# Revit family: Trap-FloorMounted-Vitra-OriginSeries-A45161
name_source: partatom
category: Plumbing Fixtures
revit_build: Autodesk Revit 2017 (Build: 20160225_1515(x64)
units: mm (PartAtom-declared; Revit-internal decimal feet)

## family parameters
Cut with Voids When Loaded = No
Host = Face
OmniClass Number = 23.45.55.17
OmniClass Title = Mixing Faucets
Part Type = Normal
Room Calculation Point = No
Round Connector Dimension = Use Diameter
Shared = Yes

## types (2) — shared parameters
BIMobject category = Sanitary - Taps & Mixers
CW Connection = Yes
Connection Diameter (mm) = 10 mm  [stored 0.0328084 ft]
Default Elevation = 850 mm  [stored 2.78871 ft]
Depth(mm) = 340 mm  [stored 1.11549 ft]
Description = Plural Floor Siphon Set - Long
Design country = Turkey
HW Connection = Yes
Height(mm) = 715 mm
IFC Classification = Sanitary Terminal
Manufacturer = Vitra
Manufacturer name = Vitra
Masterformat 2014 Code = 22 13 16
Masterformat 2014 Description = Sanitary Waste and Vent Piping
MountingType = Floor Mounted
NBS Referans Code = 31-76
NBS Referans Description = Sanitary Dispensing And Disposal Units
Nominal height = 0.000
Nominal width = 0.000
Number Of Connections = 2 mm  [stored 0.00656168 ft]
OmniClass Code = 23-21 23 27
OmniClass Description = Residential Waste Disposal Units
Product Type = Trap
Product certification = https://vitraglobal.com
Product data url = https://www.vitra.com.tr
Product family = Origin
Product group = Origin Trap
Technical description = https://www.vitra.com.tr
UNSPSC Code = 301815
UNSPSC Description = Sanitary ware
URL = https://vitraglobal.com
Uniclass 1.4 Code = L7218
Uniclass 1.4 Description = Sanitary disposal units
Uniclass 2.0 Code = PR-31-76
Uniclass 2.0 Description = Sanitary Dispensing And Disposal Units
Uniclass 2015 Code = Pr_60_45_90
Uniclass 2015 Name = Wastewater and water mixer products
Uniformat II Code = D2010
Uniformat II Description = Plumbing Fixtures
Warranty Period (Year) = 10 Years
Weight Net (kg) = 9,130
Width(mm) = 120 mm  [stored 0.393701 ft]
Youtube = https://www.youtube.com
zero-valued in all types: Cost

## per-type parameters (varying)
| type | Article No. (default) | Coating Material | Color | Model | Product SKU |
| Trap-FloorMounted-Vitra-OriginSeries(Chrome)-A45161 | A45161 | Vitra-Chrome | Chrome | A45161 | A45161 |
| Trap-FloorMounted-Vitra-OriginSeries(Black)-A4516136 | A4516136 | Vitra-MatteBlack | Matte Black | A4516136 | A4516136 |

note: [stored X ft] marks values corroborated as IEEE doubles in the binary element streams (Revit-internal decimal feet)

## geometry (parser evidence)
native form markers: Sweep x3
no freeform markers — native parametric forms only
